# Revit family: YGNIS_Recuperador humos Totaleco Bi etapa
name_source: partatom
category: Equipos mecánicos
revit_build: Autodesk Revit 2016 (Build: 20150220_1215(x64)
units: mm (PartAtom-declared; Revit-internal decimal feet)

## family parameters
Compartido = No
Corte con vacíos al cargar = No
Cota de conector redondo = Diámetro de uso
Número OmniClass = 23.75.00.00
Punto de cálculo de habitación = No
Se basa en plano de trabajo = No
Siempre vertical = Sí
Tipo de pieza = Normal
Título OmniClass = Climate Control (HVAC)

## types (7) — shared parameters
Altura patas = 58 mm
Asas = 299.52 mm
Código de montaje = D3090
Descripción = Recuperador de humos con extractor incorporado de 400 a 1430 KW
Fabricante = YGNIS Atlantic
Material = Acero
Material tomas = Acero azul
P = 70 mm  [stored 0.229659 ft]
Q = 119 mm
ø condensados = 32 mm  [stored 0.104987 ft]
ø entrada/salida ACS = 50.8 mm  [stored 0.166667 ft]
ø toma de vaciado = 12.7 mm  [stored 0.0416667 ft]
ø válvula de seguridad = 12.7 mm  [stored 0.0416667 ft]

## per-type parameters (varying)
- T1 Bi: A, anchura=820 mm; ACS Biplano=Sí; ACS Uniplano=No; B, altura=1210 mm; C, profundidad=538 mm; Caudal mínimo=3 m³/h; D=1055 mm; D empalmes=125 mm  [stored 0.410105 ft]; E entrada humos=200 mm  [stored 0.656168 ft]; E.2=195 mm  [stored 0.639764 ft]; F=215 mm; G salida humos=200 mm  [stored 0.656168 ft]; G.2=195 mm  [stored 0.639764 ft]; H=628 mm; I=224 mm  [stored 0.734908 ft]; J=448 mm; K=621 mm; L=108 mm  [stored 0.354331 ft]; M=203 mm  [stored 0.66601 ft]; Modelo=Totaleco 3T Bi; N=180 mm  [stored 0.590551 ft]; N.2=175 mm  [stored 0.574147 ft]; Potencia nominal=400 kW; R=263 mm  [stored 0.862861 ft]; R hueco entrada humos=107.5 mm; S=468 mm; T=468 mm; ø impulsión/retorno=65 mm  [stored 0.213255 ft]
- T4 Bi: A, anchura=1039 mm; ACS Biplano=Sí; ACS Uniplano=No; B, altura=1615 mm; C, profundidad=538 mm; Caudal mínimo=8 m³/h; D=1385 mm; D empalmes=160 mm  [stored 0.524934 ft]; E entrada humos=350 mm; E.2=345 mm; F=300 mm; G salida humos=300 mm; G.2=295 mm  [stored 0.967848 ft]; H=782 mm; I=306 mm; J=448 mm; K=840 mm; L=143 mm; M=292 mm  [stored 0.958005 ft]; Modelo=Totaleco 4T Bi; N=250 mm  [stored 0.82021 ft]; N.2=245 mm  [stored 0.803806 ft]; Potencia nominal=620 kW; R=263 mm  [stored 0.862861 ft]; R hueco entrada humos=182.5 mm  [stored 0.598753 ft]; S=603 mm; T=603 mm; ø impulsión/retorno=100 mm  [stored 0.328084 ft]
- T3 Bi: A, anchura=1295 mm; ACS Biplano=Sí; ACS Uniplano=No; B, altura=1390 mm; C, profundidad=538 mm; Caudal mínimo=6 m³/h; D=1185 mm; D empalmes=125 mm  [stored 0.410105 ft]; E entrada humos=300 mm; E.2=295 mm  [stored 0.967848 ft]; F=270 mm  [stored 0.885827 ft]; G salida humos=250 mm  [stored 0.82021 ft]; G.2=245 mm  [stored 0.803806 ft]; H=708 mm; I=224 mm  [stored 0.734908 ft]; J=448 mm; K=1096 mm; L=138 mm  [stored 0.452756 ft]; M=259 mm  [stored 0.849738 ft]; Modelo=Totaleco 7T Bi; N=200 mm  [stored 0.656168 ft]; N.2=195 mm  [stored 0.639764 ft]; Potencia nominal=620 kW; R=263 mm  [stored 0.862861 ft]; R hueco entrada humos=157.5 mm  [stored 0.516732 ft]; S=548 mm; T=548 mm; ø impulsión/retorno=65 mm  [stored 0.213255 ft]
- T10 Bi: A, anchura=1427 mm; ACS Biplano=No; ACS Uniplano=Sí; B, altura=1950 mm; C, profundidad=650 mm; Caudal mínimo=19 m³/h; D=1645 mm; D empalmes=185 mm  [stored 0.606955 ft]; E entrada humos=500 mm; E.2=495 mm; F=350 mm; G salida humos=400 mm; G.2=395 mm; H=980 mm; I=280 mm  [stored 0.918635 ft]; J=560 mm; K=1278 mm; L=143 mm; M=343 mm; Modelo=Totaleco 10T Bi; N=350 mm; N.2=345 mm; Potencia nominal=1430 kW; R=309 mm; R hueco entrada humos=257.5 mm  [stored 0.844816 ft]; S=670 mm; T=767 mm; ø impulsión/retorno=125 mm  [stored 0.410105 ft]
- T7 Bi: A, anchura=1360 mm; ACS Biplano=Sí; ACS Uniplano=No; B, altura=1720 mm; C, profundidad=538 mm; Caudal mínimo=12 m³/h; D=1465 mm; D empalmes=160 mm  [stored 0.524934 ft]; E entrada humos=400 mm; E.2=395 mm; F=330 mm; G salida humos=350 mm; G.2=345 mm; H=837 mm; I=306 mm; J=448 mm; K=1161 mm; L=146 mm  [stored 0.479003 ft]; M=340 mm; Modelo=Totaleco 7T Bi; N=250 mm  [stored 0.82021 ft]; N.2=245 mm  [stored 0.803806 ft]; Potencia nominal=940 kW; R=263 mm  [stored 0.862861 ft]; R hueco entrada humos=207.5 mm  [stored 0.680774 ft]; S=658 mm; T=658 mm; ø impulsión/retorno=100 mm  [stored 0.328084 ft]
- T2 Bi: A, anchura=1015 mm; ACS Biplano=Sí; ACS Uniplano=No; B, altura=1295 mm; C, profundidad=538 mm; Caudal mínimo=4 m³/h; D=1115 mm; D empalmes=125 mm  [stored 0.410105 ft]; E entrada humos=250 mm  [stored 0.82021 ft]; E.2=245 mm  [stored 0.803806 ft]; F=250 mm  [stored 0.82021 ft]; G salida humos=200 mm  [stored 0.656168 ft]; G.2=195 mm  [stored 0.639764 ft]; H=663 mm; I=224 mm  [stored 0.734908 ft]; J=448 mm; K=816 mm; L=123 mm  [stored 0.403543 ft]; M=228 mm  [stored 0.748031 ft]; Modelo=Totaleco 7T Bi; N=180 mm  [stored 0.590551 ft]; N.2=175 mm  [stored 0.574147 ft]; Potencia nominal=620 kW; R=263 mm  [stored 0.862861 ft]; R hueco entrada humos=132.5 mm; S=503 mm; T=503 mm; ø impulsión/retorno=65 mm  [stored 0.213255 ft]
- T14 Bi: A, anchura=1577 mm; ACS Biplano=No; ACS Uniplano=Sí; B, altura=1950 mm; C, profundidad=706 mm; Caudal mínimo=25 m³/h; D=1645 mm; D empalmes=185 mm  [stored 0.606955 ft]; E entrada humos=500 mm; E.2=495 mm; F=350 mm; G salida humos=400 mm; G.2=395 mm; H=980 mm; I=280 mm  [stored 0.918635 ft]; J=616 mm; K=1428 mm; L=143 mm; M=337 mm; Modelo=Totaleco 10T Bi; N=350 mm; N.2=345 mm; Potencia nominal=1430 kW; R=365 mm; R hueco entrada humos=257.5 mm  [stored 0.844816 ft]; S=670 mm; T=767 mm; ø impulsión/retorno=125 mm  [stored 0.410105 ft]

note: [stored X ft] marks values corroborated as IEEE doubles in the binary element streams (Revit-internal decimal feet)
